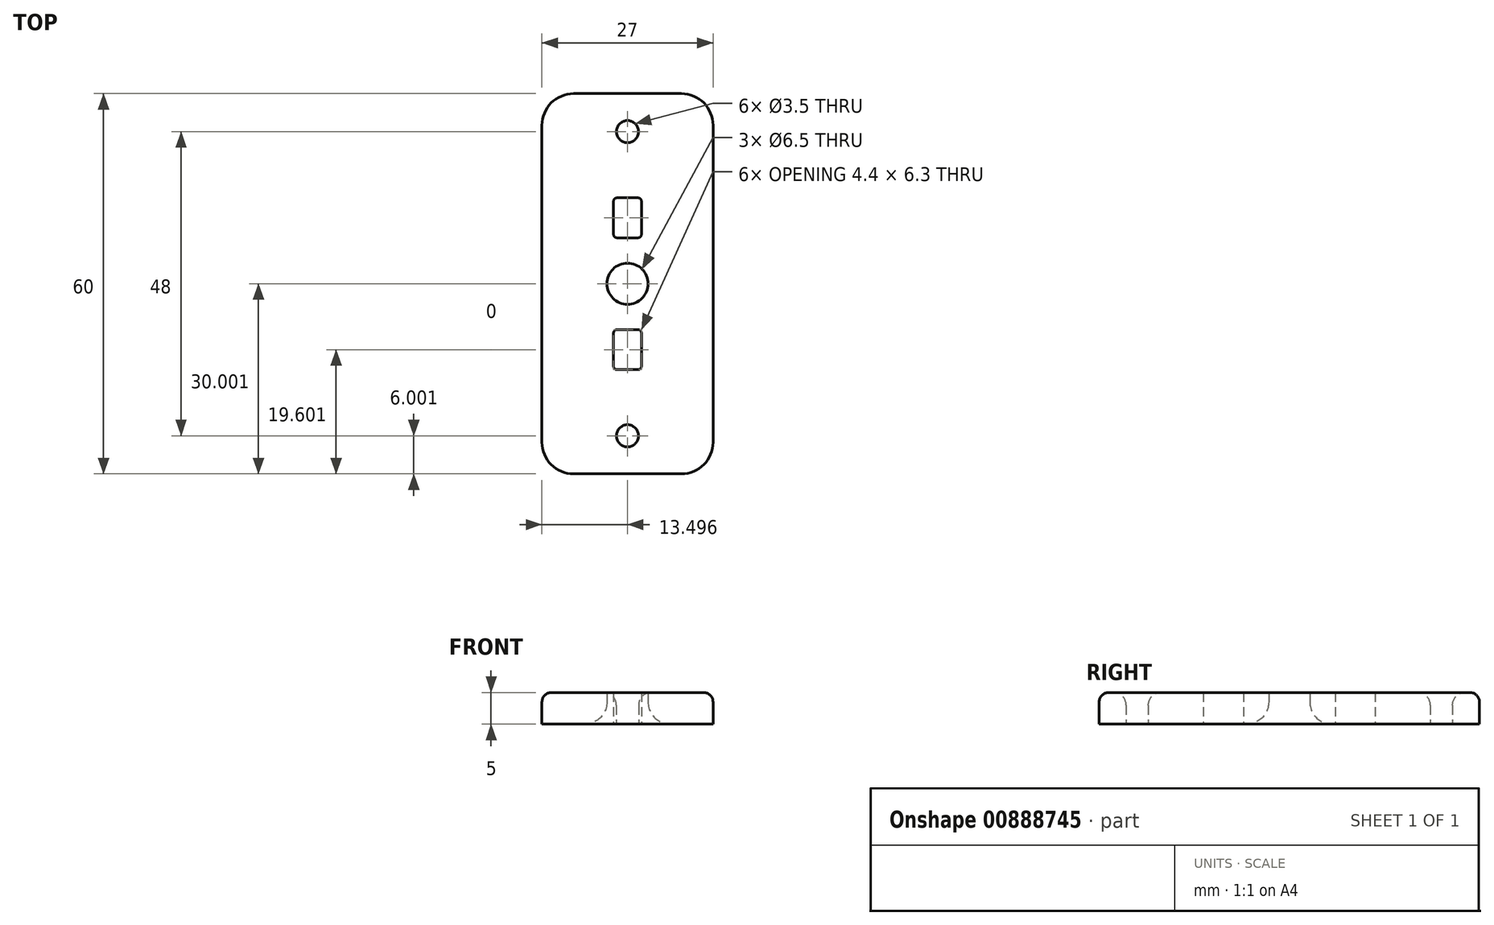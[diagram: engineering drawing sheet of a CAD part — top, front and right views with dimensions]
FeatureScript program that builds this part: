
annotation { "Feature Type Name" : "Feature", "Feature Type Description" : "" }
export const myFeature = defineFeature(function(context is Context, id is Id, definition is map)
    precondition{}
    {
        {
            var Q0;
            Q0=qCreatedBy(makeId("Top.planeOp"),FACE);
            var sketch = newSketch(context, id + "F0", { "sketchPlane" : qUnion([Q0])});
            skLineSegment(sketch, "E0", {"start": v(-17.32, -23.9) * mm, "end": v(-17.32, 26.1) * mm});
            skLineSegment(sketch, "E1", {"start": v(4.68, 31.1) * mm, "end": v(-12.32, 31.1) * mm});
            skLineSegment(sketch, "E2", {"start": v(9.68, 26.1) * mm, "end": v(9.68, -23.9) * mm});
            skLineSegment(sketch, "E3", {"start": v(-12.32, -28.9) * mm, "end": v(4.68, -28.9) * mm});
            skPoint(sketch, "E4.visualSharp", {"position": v(-17.32, -28.9) * mm});
            skArc(sketch, "E4.filletArc", {"start": v(-17.32, -23.9) * mm, "mid": v(-15.86, -27.44) * mm, "end": v(-12.32, -28.9) * mm});
            skPoint(sketch, "E5.visualSharp", {"position": v(9.68, -28.9) * mm});
            skArc(sketch, "E5.filletArc", {"start": v(4.68, -28.9) * mm, "mid": v(8.21, -27.44) * mm, "end": v(9.68, -23.9) * mm});
            skPoint(sketch, "E6.visualSharp", {"position": v(9.68, 31.1) * mm});
            skArc(sketch, "E6.filletArc", {"start": v(9.68, 26.1) * mm, "mid": v(8.21, 29.63) * mm, "end": v(4.68, 31.1) * mm});
            skPoint(sketch, "E7.visualSharp", {"position": v(-17.32, 31.1) * mm});
            skArc(sketch, "E7.filletArc", {"start": v(-12.32, 31.1) * mm, "mid": v(-15.86, 29.63) * mm, "end": v(-17.32, 26.1) * mm});
            skLineSegment(sketch, "E8", {"start": v(-3.82, -28.9) * mm, "end": v(-3.82, 31.1) * mm});
            skLineSegment(sketch, "E9", {"start": v(-3.82, 1.1) * mm, "end": v(9.68, 0) * mm});
            skCircle(sketch, "E10", {"center": v(-3.82, 1.1) * mm, "radius": 3.25 * mm});
            skLineSegment(sketch, "E11", {"start": v(-3.82, 4.34) * mm, "end": v(-3.82, 8.34) * mm});
            skLineSegment(sketch, "E12", {"start": v(-2.15, 8.34) * mm, "end": v(-3.82, 8.34) * mm});
            skLineSegment(sketch, "E13", {"start": v(-3.82, 8.34) * mm, "end": v(-5.5, 8.34) * mm});
            skLineSegment(sketch, "E14", {"start": v(-6.02, 8.87) * mm, "end": v(-6.02, 14.11) * mm});
            skLineSegment(sketch, "E15", {"start": v(-5.5, 14.64) * mm, "end": v(-2.15, 14.64) * mm});
            skLineSegment(sketch, "E16", {"start": v(-1.62, 8.87) * mm, "end": v(-1.62, 14.11) * mm});
            skLineSegment(sketch, "E17", {"start": v(-3.82, -2.16) * mm, "end": v(-3.82, -6.16) * mm});
            skLineSegment(sketch, "E18", {"start": v(-3.82, -6.16) * mm, "end": v(-5.5, -6.16) * mm});
            skLineSegment(sketch, "E19", {"start": v(-6.02, -6.69) * mm, "end": v(-6.02, -11.93) * mm});
            skLineSegment(sketch, "E20", {"start": v(-5.5, -12.46) * mm, "end": v(-2.15, -12.46) * mm});
            skLineSegment(sketch, "E21", {"start": v(-1.62, -11.93) * mm, "end": v(-1.62, -6.69) * mm});
            skLineSegment(sketch, "E22", {"start": v(-3.82, -6.16) * mm, "end": v(-2.15, -6.16) * mm});
            skPoint(sketch, "E23.visualSharp", {"position": v(-1.62, -12.46) * mm});
            skArc(sketch, "E23.filletArc", {"start": v(-2.15, -12.46) * mm, "mid": v(-1.78, -12.3) * mm, "end": v(-1.62, -11.93) * mm});
            skPoint(sketch, "E24.visualSharp", {"position": v(-6.02, -12.46) * mm});
            skArc(sketch, "E24.filletArc", {"start": v(-6.02, -11.93) * mm, "mid": v(-5.87, -12.3) * mm, "end": v(-5.5, -12.46) * mm});
            skPoint(sketch, "E25.visualSharp", {"position": v(-6.02, -6.16) * mm});
            skArc(sketch, "E25.filletArc", {"start": v(-5.5, -6.16) * mm, "mid": v(-5.87, -6.31) * mm, "end": v(-6.02, -6.69) * mm});
            skPoint(sketch, "E26.visualSharp", {"position": v(-1.62, -6.16) * mm});
            skArc(sketch, "E26.filletArc", {"start": v(-1.62, -6.69) * mm, "mid": v(-1.78, -6.31) * mm, "end": v(-2.15, -6.16) * mm});
            skPoint(sketch, "E27.visualSharp", {"position": v(-1.62, 14.64) * mm});
            skArc(sketch, "E27.filletArc", {"start": v(-1.62, 14.11) * mm, "mid": v(-1.78, 14.49) * mm, "end": v(-2.15, 14.64) * mm});
            skPoint(sketch, "E28.visualSharp", {"position": v(-6.02, 14.64) * mm});
            skArc(sketch, "E28.filletArc", {"start": v(-5.5, 14.64) * mm, "mid": v(-5.87, 14.49) * mm, "end": v(-6.02, 14.11) * mm});
            skPoint(sketch, "E29.visualSharp", {"position": v(-6.02, 8.34) * mm});
            skArc(sketch, "E29.filletArc", {"start": v(-6.02, 8.87) * mm, "mid": v(-5.87, 8.5) * mm, "end": v(-5.5, 8.34) * mm});
            skPoint(sketch, "E30.visualSharp", {"position": v(-1.62, 8.34) * mm});
            skArc(sketch, "E30.filletArc", {"start": v(-2.15, 8.34) * mm, "mid": v(-1.78, 8.5) * mm, "end": v(-1.62, 8.87) * mm});
            skLineSegment(sketch, "E31", {"start": v(-3.82, 31.1) * mm, "end": v(-3.82, 25.1) * mm});
            skCircle(sketch, "E32", {"center": v(-3.82, 25.1) * mm, "radius": 1.75 * mm});
            skLineSegment(sketch, "E33", {"start": v(-3.82, -28.9) * mm, "end": v(-3.82, -22.9) * mm});
            skCircle(sketch, "E34", {"center": v(-3.82, -22.9) * mm, "radius": 1.75 * mm});
            skSolve(sketch);
        }
        {
            var Q0;
            Q0 = qSketchRegion(id + "F0", true);
            extrude(context, id + "F1", {"entities" : qUnion([Q0]), "depth" : 5 * mm, "offsetDistance" : 25 * mm});
        }
        {
            var Q0;
            Q0=makeQuery(id+"F1.opExtrude","CAP_EDGE",EDGE,{"disambiguationData":[OSD([sQuery(id+"F0.wireOp",EDGE,"E34")])],"isStart":false});
            var Q1;
            Q1=makeQuery(id+"F1.opExtrude","CAP_EDGE",EDGE,{"disambiguationData":[OSD([sQuery(id+"F0.wireOp",EDGE,"E32")])],"isStart":false});
            fillet(context, id + "F2", {"entities" : qUnion([Q0, Q1]), "radius" : 2 * mm, "tangentPropagation" : true, "allowEdgeOverflow" : false});
        }
        {
            var Q0;
            Q0=makeQuery(id+"F1.opExtrude","CAP_EDGE",EDGE,{"disambiguationData":[OSD([sQuery(id+"F0.wireOp",EDGE,"E10")])],"isStart":true});
            fillet(context, id + "F3", {"entities" : qUnion([Q0]), "radius" : 3.5 * mm, "tangentPropagation" : true, "allowEdgeOverflow" : false});
        }
        {
            var Q0;
            Q0=makeQuery(id+"F1.opExtrude","CAP_EDGE",EDGE,{"disambiguationData":[OSD([sQuery(id+"F0.wireOp",EDGE,"E0")])],"isStart":false});
            fillet(context, id + "F4", {"entities" : qUnion([Q0]), "radius" : 1.5 * mm, "tangentPropagation" : true, "allowEdgeOverflow" : false});
        }
    });
